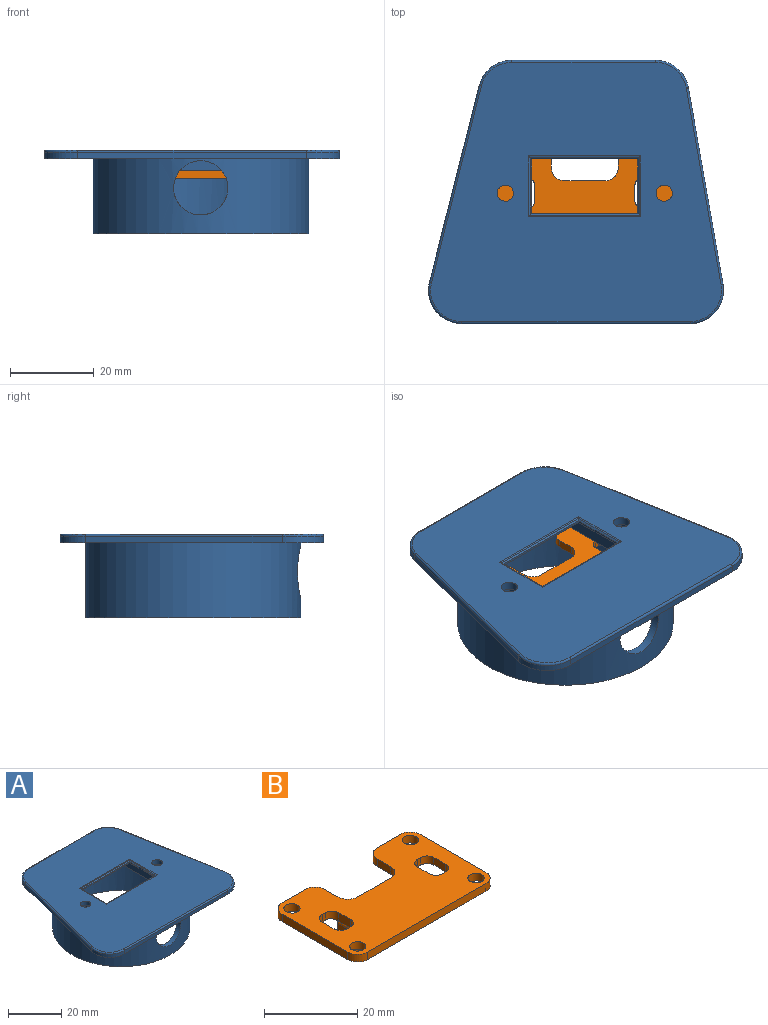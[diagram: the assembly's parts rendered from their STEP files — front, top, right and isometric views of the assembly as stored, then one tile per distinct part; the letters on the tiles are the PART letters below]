
ASSEMBLY  parts=2 mates=1
PART A: 89 faces, bbox 71.9x64.4x20 mm
  f0: cylinder r=23.8mm len=47.6mm, axis (0,0,1), area 2425.5mm2, adj f2,f3,f4,f5,f6,f7,f10,f27
  f1: cylinder r=25.8mm len=51.6mm, axis (0,0,1), area 2783.8mm2, adj f26,f27,f88
  f2: plane 47.6x30.4mm, normal (0,0,-1), area 374.8mm2, adj f0,f28,f29,f30,f31,f32,f33,f34
  f3: plane 39.92x10.88mm, normal (0,0,-1), area 236.8mm2, adj f0,f36,f37,f38,f39,f40
  f4: plane 8.05x1.76mm, normal (0,0,-1), area 13.8mm2, adj f0,f41,f42,f43
  f5: plane 8.05x1.9mm, normal (0,0,-1), area 14.8mm2, adj f0,f44,f45,f46
  f6: plane 39.87x10.8mm, normal (0,0,-1), area 236.4mm2, adj f0,f47,f48,f49,f50,f51
  f7: plane 8.05x1.9mm, normal (0,0,-1), area 14.8mm2, adj f0,f52,f53,f54
  f8: plane 6.4x6.2mm, normal (0,0,-1), area 27.7mm2, adj f21,f28,f29,f30,f59
  f9: plane 6.4x6.2mm, normal (0,0,-1), area 27.7mm2, adj f22,f31,f32,f33,f62
  f10: plane 8.05x1.9mm, normal (0,0,-1), area 14.8mm2, adj f0,f34,f35,f63
  f11: plane 13.1x0.5mm, normal (1,0,0), area 6.6mm2, adj f12,f24,f70,f71
  f12: plane 25.4x0.5mm, normal (0,-1,0), area 12.7mm2, adj f11,f13,f70,f73
  f13: plane 13.1x0.5mm, normal (-1,0,0), area 6.6mm2, adj f12,f24,f70,f74
  f14: plane 47.04x8.3mm, normal (0.98,0.17,0), area 71.7mm2, adj f15,f23,f26,f82
  f15: cylinder r=8mm len=7.88mm, axis (0,0,-1), area 16.8mm2, adj f14,f16,f26,f81
  f16: plane 34.42x1.5mm, normal (0,1,0), area 51.6mm2, adj f15,f17,f26,f79
  f17: cylinder r=8mm len=7.76mm, axis (0,0,-1), area 15.9mm2, adj f16,f18,f26,f77
  f18: plane 47.04x11.91mm, normal (-0.97,0.25,0), area 72.8mm2, adj f17,f19,f26,f75
  f19: cylinder r=8mm len=9.96mm, axis (0,0,-1), area 21.8mm2, adj f18,f20,f26,f76
  f20: plane 54.62x1.5mm, normal (0,-1,0), area 81.9mm2, adj f19,f23,f26,f78
  f21: cylinder r=1.95mm len=3.9mm, axis (0,0,-1), area 24.5mm2, adj f8,f25
  f22: cylinder r=1.95mm len=3.9mm, axis (0,0,-1), area 24.5mm2, adj f9,f25
  f23: cylinder r=8mm len=9.39mm, axis (0,0,-1), area 20.9mm2, adj f14,f20,f26,f80
  f24: plane 25.4x0.5mm, normal (0,1,0), area 12.7mm2, adj f11,f13,f70,f72
  f25: plane 69.62x62.04mm, normal (0,0,1), area 3248mm2, adj f21,f22,f75,f76,f77,f78,f79,f80
  f26: plane 70.62x63.04mm, normal (0,0,-1), area 1686.9mm2, adj f1,f14,f15,f16,f17,f18,f19,f20
  f27: plane 51.6x51.6mm, normal (0,0,-1), area 311.6mm2, adj f0,f1
  f28: plane 6.2x2.8mm, normal (1,0,0), area 17.4mm2, adj f2,f8,f29,f59
  f29: plane 6.4x2.8mm, normal (0,-1,0), area 17.9mm2, adj f2,f8,f28,f30
  f30: plane 6.2x2.8mm, normal (-1,0,0), area 17.4mm2, adj f2,f8,f29,f59
  f31: plane 6.2x2.8mm, normal (1,0,0), area 17.4mm2, adj f2,f9,f32,f62
  f32: plane 6.4x2.8mm, normal (0,-1,0), area 17.9mm2, adj f2,f9,f31,f33
  f33: plane 6.2x2.8mm, normal (-1,0,0), area 17.4mm2, adj f2,f9,f32,f62
  f34: plane 2.8x1.9mm, normal (1,0,0), area 5.3mm2, adj f2,f10,f35,f63
  f35: plane 7.55x2.8mm, normal (0,-1,0), area 21.1mm2, adj f0,f2,f10,f34
  f36: plane 4.74x2.8mm, normal (0,1,0), area 13.3mm2, adj f0,f2,f3,f37
  f37: plane 2.8x2.2mm, normal (1,0,0), area 6.2mm2, adj f2,f3,f36,f38
  f38: plane 30.4x2.8mm, normal (0,1,0), area 85.1mm2, adj f2,f3,f37,f39
  f39: plane 2.8x2.28mm, normal (-1,0,0), area 6.4mm2, adj f2,f3,f38,f40
  f40: plane 4.78x2.8mm, normal (0,1,0), area 13.4mm2, adj f0,f2,f3,f39
  f41: plane 7.59x2.8mm, normal (0,-1,0), area 21.2mm2, adj f0,f2,f4,f42
  f42: plane 2.8x1.76mm, normal (-1,0,0), area 4.9mm2, adj f2,f4,f41,f43
  f43: plane 8.05x2.8mm, normal (0,1,0), area 22.5mm2, adj f0,f2,f4,f42
  f44: plane 8.05x2.8mm, normal (0,-1,0), area 22.5mm2, adj f0,f2,f5,f45
  f45: plane 2.8x1.9mm, normal (-1,0,0), area 5.3mm2, adj f2,f5,f44,f46
  f46: plane 7.55x2.8mm, normal (0,1,0), area 21.1mm2, adj f0,f2,f5,f45
  f47: plane 4.74x2.8mm, normal (0,-1,0), area 13.3mm2, adj f0,f2,f6,f48
  f48: plane 2.8x2.2mm, normal (-1,0,0), area 6.2mm2, adj f2,f6,f47,f49
  f49: plane 30.4x2.8mm, normal (0,-1,0), area 69.3mm2, adj f2,f6,f48,f50,f87
  f50: plane 2.8x2.2mm, normal (1,0,0), area 6.2mm2, adj f2,f6,f49,f51
  f51: plane 4.74x2.8mm, normal (0,-1,0), area 13.3mm2, adj f0,f2,f6,f50
  f52: plane 7.55x2.8mm, normal (0,1,0), area 21.1mm2, adj f0,f2,f7,f53
  f53: plane 2.8x1.9mm, normal (1,0,0), area 5.3mm2, adj f2,f7,f52,f54
  f54: plane 8.05x2.8mm, normal (0,-1,0), area 22.5mm2, adj f0,f2,f7,f53
  f55: plane 27.4x3.8mm, normal (1,0,0), area 104.1mm2, adj f2,f56,f64,f70
  f56: plane 27.4x3.8mm, normal (0,-1,0), area 104.1mm2, adj f2,f55,f57,f70
  f57: plane 27.4x3.8mm, normal (-1,0,0), area 104.1mm2, adj f2,f56,f64,f70
  f58: cylinder r=1.5mm len=3mm, axis (0,0,1), area 26.4mm2, adj f2,f69
  f59: plane 6.4x2.8mm, normal (0,1,0), area 17.9mm2, adj f2,f8,f28,f30
  f60: cylinder r=1.5mm len=3mm, axis (0,0,1), area 26.4mm2, adj f2,f68
  f61: cylinder r=1.5mm len=3mm, axis (0,0,1), area 26.4mm2, adj f2,f67
  f62: plane 6.4x2.8mm, normal (0,1,0), area 17.9mm2, adj f2,f9,f31,f33
  f63: plane 8.05x2.8mm, normal (0,1,0), area 22.5mm2, adj f0,f2,f10,f34
  f64: plane 27.4x3.8mm, normal (0,1,0), area 88.3mm2, adj f2,f55,f57,f70,f87
  f65: cylinder r=1.5mm len=3mm, axis (0,0,1), area 26.4mm2, adj f2,f66
  f66: plane 3x3mm, normal (0,0,-1), area 7.1mm2, adj f65
  f67: plane 3x3mm, normal (0,0,-1), area 7.1mm2, adj f61
  f68: plane 3x3mm, normal (0,0,-1), area 7.1mm2, adj f60
  f69: plane 3x3mm, normal (0,0,-1), area 7.1mm2, adj f58
  f70: plane 27.4x27.4mm, normal (0,0,-1), area 418mm2, adj f11,f12,f13,f24,f55,f56,f57,f64
  f71: plane 13.81x0.35mm, normal (0.71,0,0.71), area 6.7mm2, adj f11,f72,f73,f83
  f72: plane 26.11x0.35mm, normal (0,0.71,0.71), area 12.9mm2, adj f24,f71,f74,f85
  f73: plane 26.11x0.35mm, normal (0,-0.71,0.71), area 12.9mm2, adj f12,f71,f74,f84
  f74: plane 13.81x0.35mm, normal (-0.71,0,0.71), area 6.7mm2, adj f13,f72,f73,f86
  f75: cylinder r=0.5mm len=47.17mm, axis (0.25,0.97,0), area 38.1mm2, adj f18,f25,f76,f77
  f76: torus R=7.5mm, axis (0,0,1), area 11.2mm2, adj f19,f25,f75,f78
  f77: torus R=7.5mm, axis (0,0,1), area 8.1mm2, adj f17,f25,f75,f79
  f78: cylinder r=0.5mm len=54.62mm, axis (-1,0,0), area 42.9mm2, adj f20,f25,f76,f80
  f79: cylinder r=0.5mm len=34.42mm, axis (1,0,0), area 27mm2, adj f16,f25,f77,f81
  f80: torus R=7.5mm, axis (0,0,1), area 10.7mm2, adj f23,f25,f78,f82
  f81: torus R=7.5mm, axis (0,0,1), area 8.6mm2, adj f15,f25,f79,f82
  f82: cylinder r=0.5mm len=47.13mm, axis (0.17,-0.98,0), area 37.5mm2, adj f14,f25,f80,f81
  f83: cylinder r=0.5mm len=14.51mm, axis (0,-1,0), area 5.6mm2, adj f25,f71,f84,f85
  f84: cylinder r=0.5mm len=26.81mm, axis (-1,0,0), area 10.4mm2, adj f25,f73,f83,f86
  f85: cylinder r=0.5mm len=26.81mm, axis (1,0,0), area 10.4mm2, adj f25,f72,f83,f86
  f86: cylinder r=0.5mm len=14.51mm, axis (0,1,0), area 5.6mm2, adj f25,f74,f84,f85
  f87: cylinder r=6.5mm len=9.92mm, axis (0,1,0), area 16.9mm2, adj f2,f49,f64
  f88: cylinder r=6.5mm len=13mm, axis (0,1,0), area 83.1mm2, adj f0,f1
PART B: 60 faces, bbox 42x26x11 mm
  f0: plane 6x5mm, normal (-1,0,0), area 30mm2, adj f43,f45,f52,f56
  f1: plane 6x5mm, normal (1,0,0), area 30mm2, adj f40,f42,f46,f57
  f2: plane 42x26mm, normal (0,0,-1), area 710mm2, adj f3,f4,f5,f6,f7,f8,f9,f10
  f3: plane 7x2mm, normal (0,1,0), area 14mm2, adj f2,f4,f38,f39
  f4: cylinder r=3mm len=3mm, axis (0,0,-1), area 9.4mm2, adj f2,f3,f5,f39
  f5: plane 20x2mm, normal (-1,0,0), area 40mm2, adj f2,f4,f6,f39
  f6: cylinder r=3mm len=3mm, axis (0,0,-1), area 9.4mm2, adj f2,f5,f7,f39
  f7: plane 36x2mm, normal (0,-1,0), area 72mm2, adj f2,f6,f8,f39
  f8: cylinder r=3mm len=3mm, axis (0,0,-1), area 9.4mm2, adj f2,f7,f9,f39
  f9: plane 20x2mm, normal (1,0,0), area 40mm2, adj f2,f8,f10,f39
  f10: cylinder r=3mm len=3mm, axis (0,0,-1), area 9.4mm2, adj f2,f9,f11,f39
  f11: plane 7x2mm, normal (0,1,0), area 14mm2, adj f2,f10,f12,f39
  f12: cylinder r=3mm len=3mm, axis (0,0,-1), area 9.4mm2, adj f2,f11,f13,f39
  f13: plane 4x2mm, normal (-1,0,0), area 8mm2, adj f2,f12,f14,f39
  f14: cylinder r=3mm len=3mm, axis (0,0,-1), area 9.5mm2, adj f2,f13,f15,f39,f50,f52
  f15: plane 10x2mm, normal (0,1,0), area 20mm2, adj f2,f14,f16,f39
  f16: cylinder r=3mm len=3mm, axis (0,0,-1), area 9.5mm2, adj f2,f15,f17,f39,f46,f48
  f17: plane 4x2mm, normal (1,0,0), area 8mm2, adj f2,f16,f38,f39
  f18: cylinder r=2mm len=2mm, axis (0,0,-1), area 6.3mm2, adj f2,f19,f32,f39
  f19: plane 2x1mm, normal (0,1,0), area 2mm2, adj f2,f18,f20,f39
  f20: cylinder r=2mm len=2.27mm, axis (0,0,-1), area 6.6mm2, adj f2,f19,f21,f39,f51
  f21: plane 3.6x2.27mm, normal (1,0,0), area 8.2mm2, adj f20,f22,f39,f51
  f22: cylinder r=2mm len=2.27mm, axis (0,0,-1), area 6.6mm2, adj f2,f21,f23,f39,f51
  f23: plane 2x1mm, normal (0,-1,0), area 2mm2, adj f2,f22,f24,f39
  f24: cylinder r=2mm len=2mm, axis (0,0,-1), area 6.3mm2, adj f2,f23,f32,f39
  f25: cylinder r=2mm len=2.27mm, axis (0,0,-1), area 6.6mm2, adj f2,f26,f33,f39,f49
  f26: plane 3.6x2.27mm, normal (-1,0,0), area 8.2mm2, adj f25,f27,f39,f49
  f27: cylinder r=2mm len=2.27mm, axis (0,0,-1), area 6.6mm2, adj f2,f26,f28,f39,f49
  f28: plane 2x1mm, normal (0,1,0), area 2mm2, adj f2,f27,f29,f39
  f29: cylinder r=2mm len=2mm, axis (0,0,-1), area 6.3mm2, adj f2,f28,f30,f39
  f30: plane 3.6x2mm, normal (1,0,0), area 7.2mm2, adj f2,f29,f31,f39
  f31: cylinder r=2mm len=2mm, axis (0,0,-1), area 6.3mm2, adj f2,f30,f33,f39
  f32: plane 3.6x2mm, normal (-1,0,0), area 7.2mm2, adj f2,f18,f24,f39
  f33: plane 2x1mm, normal (0,-1,0), area 2mm2, adj f2,f25,f31,f39
  f34: cylinder r=1.75mm len=3.5mm, axis (0,0,-1), area 22mm2, adj f2,f39
  f35: cylinder r=1.75mm len=3.5mm, axis (0,0,-1), area 22mm2, adj f2,f39
  f36: cylinder r=1.75mm len=3.5mm, axis (0,0,-1), area 22mm2, adj f2,f39
  f37: cylinder r=1.75mm len=3.5mm, axis (0,0,-1), area 22mm2, adj f2,f39
  f38: cylinder r=3mm len=3mm, axis (0,0,-1), area 9.4mm2, adj f2,f3,f17,f39
  f39: plane 42x26mm, normal (0,0,1), area 816.7mm2, adj f3,f4,f5,f6,f7,f8,f9,f10
  f40: plane 7x3mm, normal (0,1,0), area 11.7mm2, adj f1,f41,f48,f54,f57,f58
  f41: plane 6x2.42mm, normal (-1,0,0), area 14.5mm2, adj f40,f42,f49,f58
  f42: plane 7x3mm, normal (0,-1,0), area 11.7mm2, adj f1,f41,f47,f54,f57,f58
  f43: plane 7x3mm, normal (0,-1,0), area 11.7mm2, adj f0,f44,f53,f55,f56,f59
  f44: plane 6x2.42mm, normal (1,0,0), area 14.5mm2, adj f43,f45,f51,f59
  f45: plane 7x3mm, normal (0,1,0), area 11.7mm2, adj f0,f44,f50,f55,f56,f59
  f46: cylinder r=2mm len=9.44mm, axis (0,1,0), area 23mm2, adj f1,f2,f16,f47,f48
  f47: cylinder r=2mm len=6mm, axis (1,0,0), area 10.8mm2, adj f2,f42,f46,f49
  f48: cylinder r=2mm len=5.44mm, axis (-1,0,0), area 10.6mm2, adj f2,f16,f40,f46,f49
  f49: cylinder r=2mm len=10mm, axis (0,-1,0), area 17.1mm2, adj f2,f25,f26,f27,f41,f47,f48
  f50: cylinder r=2mm len=5.44mm, axis (-1,0,0), area 10.6mm2, adj f2,f14,f45,f51,f52
  f51: cylinder r=2mm len=10mm, axis (0,1,0), area 17.1mm2, adj f2,f20,f21,f22,f44,f50,f53
  f52: cylinder r=2mm len=9.44mm, axis (0,-1,0), area 23mm2, adj f0,f2,f14,f50,f53
  f53: cylinder r=2mm len=6mm, axis (1,0,0), area 10.8mm2, adj f2,f43,f51,f52
  f54: plane 6x1mm, normal (1,0,0), area 6mm2, adj f40,f42,f57,f58
  f55: plane 6x1mm, normal (-1,0,0), area 6mm2, adj f43,f45,f56,f59
  f56: plane 6x1mm, normal (-0.71,0,0.71), area 8.5mm2, adj f0,f43,f45,f55
  f57: plane 6x1mm, normal (0.71,0,0.71), area 8.5mm2, adj f1,f40,f42,f54
  f58: cylinder r=5mm len=6mm, axis (0,1,0), area 34.8mm2, adj f40,f41,f42,f54
  f59: cylinder r=5mm len=6mm, axis (0,-1,0), area 34.8mm2, adj f43,f44,f45,f55
PLACE A t=(2.14,-0.27,4.97)mm
PLACE B t=(2.14,-0.27,0.17)mm
MATE fastened B.f10 <-> A.f65  axis (0,0,1) through (20.14,9.73,2.17)mm
